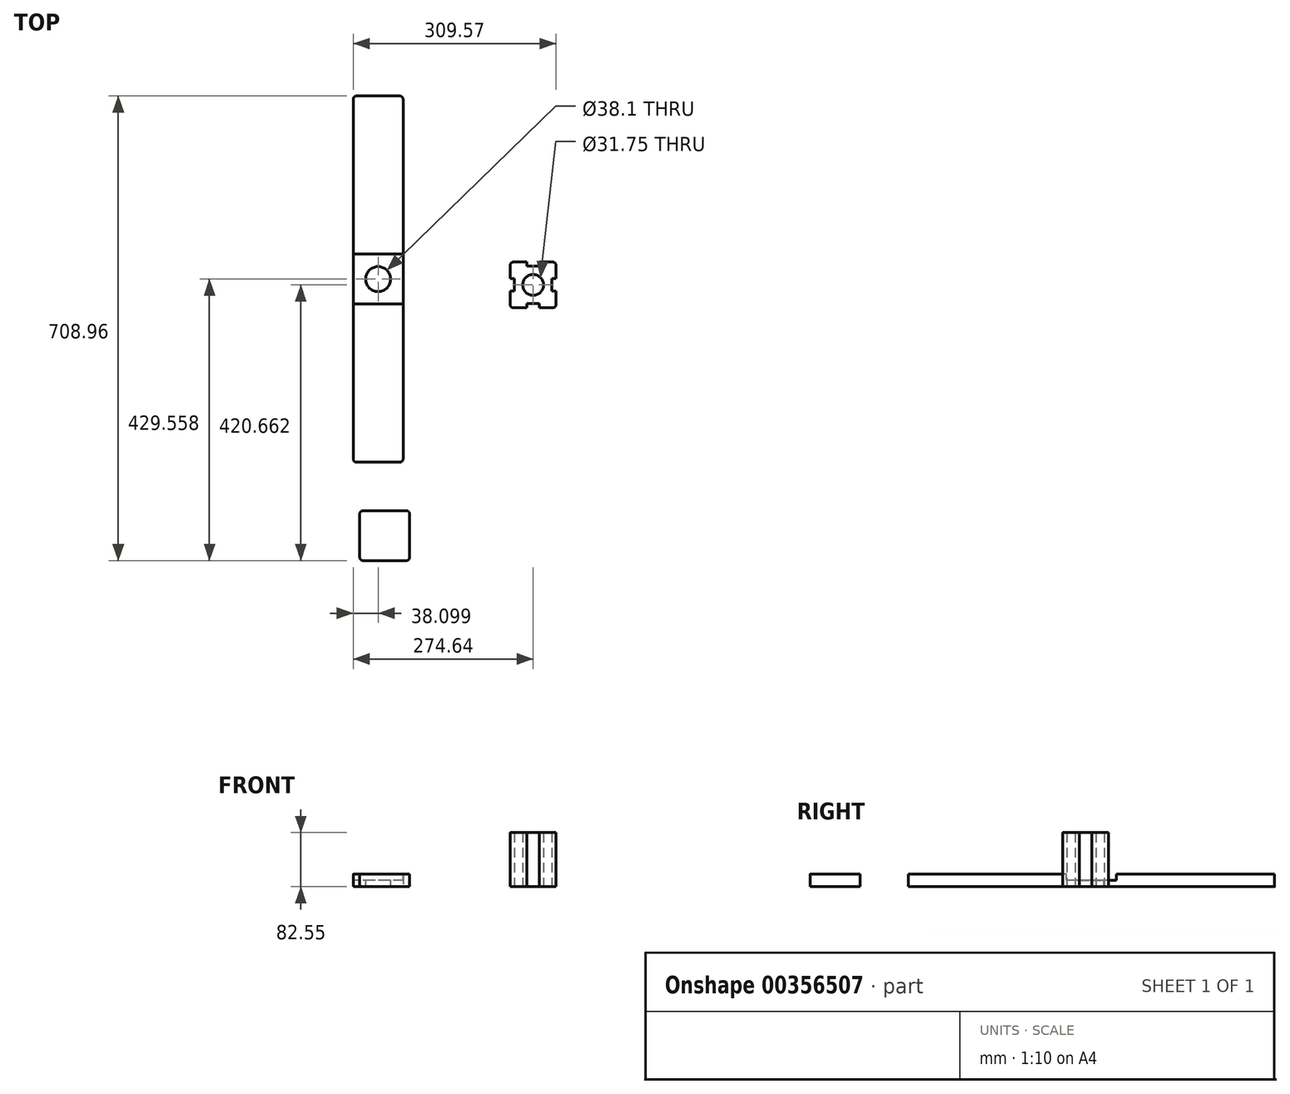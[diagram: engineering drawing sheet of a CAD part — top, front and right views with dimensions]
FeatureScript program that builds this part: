
annotation { "Feature Type Name" : "Feature", "Feature Type Description" : "" }
export const myFeature = defineFeature(function(context is Context, id is Id, definition is map)
    precondition{}
    {
        {
            assignVariable(context, id + "F0", {"name" : "BaseThickness", "anyValue" : 19.05 * mm});
        }
        {
            var Q0;
            Q0=qCreatedBy(makeId("Top.planeOp"),FACE);
            var sketch = newSketch(context, id + "F1", { "sketchPlane" : qUnion([Q0])});
            skLineSegment(sketch, "E0.bottom", {"start": v(32.09, 39.46) * mm, "end": v(57.49, 39.46) * mm});
            skLineSegment(sketch, "E0.top", {"start": v(32.09, -30.4) * mm, "end": v(57.49, -30.4) * mm});
            skLineSegment(sketch, "E0.left", {"start": v(32.09, 39.46) * mm, "end": v(32.09, 14.06) * mm});
            skLineSegment(sketch, "E0.right", {"start": v(101.94, 39.46) * mm, "end": v(101.94, 14.06) * mm});
            skLineSegment(sketch, "E1", {"start": v(32.09, 39.46) * mm, "end": v(101.94, -30.4) * mm, "construction": true});
            skCircle(sketch, "E2", {"center": v(67.01, 4.53) * mm, "radius": 15.88 * mm});
            skLineSegment(sketch, "E3.top", {"start": v(57.49, 33.1) * mm, "end": v(76.54, 33.1) * mm});
            skLineSegment(sketch, "E3.left", {"start": v(57.49, 39.46) * mm, "end": v(57.49, 33.1) * mm});
            skLineSegment(sketch, "E3.right", {"start": v(76.54, 39.46) * mm, "end": v(76.54, 33.1) * mm});
            skPoint(sketch, "E4", {"position": v(67.01, 39.46) * mm});
            skPoint(sketch, "E5", {"position": v(101.94, 4.53) * mm});
            skPoint(sketch, "E6", {"position": v(67.01, -30.4) * mm});
            skLineSegment(sketch, "E7.bottom", {"start": v(95.59, 14.06) * mm, "end": v(101.94, 14.06) * mm});
            skLineSegment(sketch, "E7.top", {"start": v(95.59, -5) * mm, "end": v(101.94, -5) * mm});
            skLineSegment(sketch, "E7.left", {"start": v(95.59, 14.06) * mm, "end": v(95.59, -5) * mm});
            skLineSegment(sketch, "E8.bottom", {"start": v(57.49, -24.04) * mm, "end": v(76.54, -24.04) * mm});
            skLineSegment(sketch, "E8.left", {"start": v(57.49, -24.04) * mm, "end": v(57.49, -30.4) * mm});
            skLineSegment(sketch, "E8.right", {"start": v(76.54, -24.04) * mm, "end": v(76.54, -30.4) * mm});
            skLineSegment(sketch, "E9.bottom", {"start": v(32.09, 14.06) * mm, "end": v(38.44, 14.06) * mm});
            skLineSegment(sketch, "E9.top", {"start": v(32.09, -5) * mm, "end": v(38.44, -5) * mm});
            skLineSegment(sketch, "E9.right", {"start": v(38.44, 14.06) * mm, "end": v(38.44, -5) * mm});
            skLineSegment(sketch, "E10.trimOffspring", {"start": v(76.54, 39.46) * mm, "end": v(101.94, 39.46) * mm});
            skLineSegment(sketch, "E11.trimOffspring", {"start": v(101.94, -5) * mm, "end": v(101.94, -30.4) * mm});
            skLineSegment(sketch, "E12.trimOffspring", {"start": v(76.54, -30.4) * mm, "end": v(101.94, -30.4) * mm});
            skLineSegment(sketch, "E13.trimOffspring", {"start": v(32.09, -5) * mm, "end": v(32.09, -30.4) * mm});
            skSolve(sketch);
        }
        {
            var Q0;
            Q0 = qSketchRegion(id + "F1", true);
            extrude(context, id + "F2", {"entities" : qUnion([Q0]), "depth" : 82.55 * mm});
        }
        {
            var Q0;
            Q0=qCreatedBy(makeId("Top.planeOp"),FACE);
            var sketch = newSketch(context, id + "F3", { "sketchPlane" : qUnion([Q0])});
            skLineSegment(sketch, "E14.bottom", {"start": v(-131.43, 292.83) * mm, "end": v(-207.63, 292.83) * mm});
            skLineSegment(sketch, "E14.top", {"start": v(-131.43, -265.97) * mm, "end": v(-207.63, -265.97) * mm});
            skLineSegment(sketch, "E14.left", {"start": v(-131.43, 292.83) * mm, "end": v(-131.43, -265.97) * mm});
            skLineSegment(sketch, "E14.right", {"start": v(-207.63, 292.83) * mm, "end": v(-207.63, -265.97) * mm});
            skLineSegment(sketch, "E15.bottom", {"start": v(-197.64, -339.93) * mm, "end": v(-121.44, -339.93) * mm});
            skLineSegment(sketch, "E15.top", {"start": v(-197.64, -416.13) * mm, "end": v(-121.44, -416.13) * mm});
            skLineSegment(sketch, "E15.left", {"start": v(-197.64, -339.93) * mm, "end": v(-197.64, -416.13) * mm});
            skLineSegment(sketch, "E15.right", {"start": v(-121.44, -339.93) * mm, "end": v(-121.44, -416.13) * mm});
            skSolve(sketch);
        }
        {
            var Q0;
            Q0 = qSketchRegion(id + "F3", true);
            extrude(context, id + "F4", {"entities" : qUnion([Q0]), "depth" : getVariable(context, 'BaseThickness')});
        }
        {
            var Q0;
            Q0=makeQuery(id+"F4.opExtrude","CAP_FACE",FACE,{"disambiguationData":[OSD([sQuery(id+"F3.wireOp",EDGE,"E14.bottom"),sQuery(id+"F3.wireOp",EDGE,"E14.top"),sQuery(id+"F3.wireOp",EDGE,"E14.left"),sQuery(id+"F3.wireOp",EDGE,"E14.right")])],"isStart":false});
            var sketch = newSketch(context, id + "F5", { "sketchPlane" : qUnion([Q0])});
            skLineSegment(sketch, "E16", {"start": v(-169.53, 292.83) * mm, "end": v(-169.53, -265.97) * mm, "construction": true});
            skPoint(sketch, "E17", {"position": v(-169.53, 13.43) * mm});
            skLineSegment(sketch, "E18", {"start": v(-131.43, 51.53) * mm, "end": v(-207.63, 51.53) * mm});
            skLineSegment(sketch, "E19", {"start": v(-131.43, 13.43) * mm, "end": v(-169.53, 13.43) * mm, "construction": true});
            skLineSegment(sketch, "E20.MirrorCS", {"start": v(-131.43, -24.67) * mm, "end": v(-207.63, -24.67) * mm});
            skLineSegment(sketch, "E21", {"start": v(-155.5, 51.53) * mm, "end": v(-155.5, -24.67) * mm, "construction": true});
            skPoint(sketch, "E22", {"position": v(-155.5, 13.43) * mm});
            skCircle(sketch, "E23", {"center": v(-169.53, 13.43) * mm, "radius": 19.05 * mm});
            skSolve(sketch);
        }
        {
            var Q0;
            Q0 = qSketchRegion(id + "F5", true);
            var Q1;
            {var subQ0=sQuery(id+"F5.wireOp",EDGE,"E18");Q1=makeQuery(id+"F5.imprint","IMPRINT",FACE,{"disambiguationData":[TD([[makeQuery(id+"F5.imprint","IMPRINT",EDGE,{"derivedFrom":subQ0}),1.0]])]});}
            extrude(context, id + "F6", {"entities" : qUnion([Q0, Q1]), "operationType" : NewBodyOperationType.REMOVE, "oppositeDirection" : true, "depth" : getVariable(context, 'BaseThickness') / 2});
        }
        {
            var Q0;
            Q0=makeQuery(id+"F4.opExtrude","SWEPT_EDGE",EDGE,{"disambiguationData":[OSD([sQuery(id+"F3.wireOp",EDGE,"E14.bottom"),sQuery(id+"F3.wireOp",EDGE,"E14.right")])]});
            var Q1;
            Q1=makeQuery(id+"F4.opExtrude","SWEPT_EDGE",EDGE,{"disambiguationData":[OSD([sQuery(id+"F3.wireOp",EDGE,"E14.bottom"),sQuery(id+"F3.wireOp",EDGE,"E14.left")])]});
            var Q2;
            Q2=makeQuery(id+"F4.opExtrude","SWEPT_EDGE",EDGE,{"disambiguationData":[OSD([sQuery(id+"F3.wireOp",EDGE,"E14.top"),sQuery(id+"F3.wireOp",EDGE,"E14.right")])]});
            var Q3;
            Q3=makeQuery(id+"F4.opExtrude","SWEPT_EDGE",EDGE,{"disambiguationData":[OSD([sQuery(id+"F3.wireOp",EDGE,"E14.top"),sQuery(id+"F3.wireOp",EDGE,"E14.left")])]});
            fillet(context, id + "F7", {"entities" : qUnion([Q0, Q1, Q2, Q3]), "radius" : 5.08 * mm, "tangentPropagation" : true, "allowEdgeOverflow" : false});
        }
        {
            var Q0;
            Q0=makeQuery(id+"F2.opExtrude","SWEPT_EDGE",EDGE,{"disambiguationData":[OSD([sQuery(id+"F1.wireOp",EDGE,"E11.trimOffspring"),sQuery(id+"F1.wireOp",EDGE,"E12.trimOffspring")])]});
            var Q1;
            Q1=makeQuery(id+"F2.opExtrude","SWEPT_EDGE",EDGE,{"disambiguationData":[OSD([sQuery(id+"F1.wireOp",EDGE,"E0.top"),sQuery(id+"F1.wireOp",EDGE,"E13.trimOffspring")])]});
            var Q2;
            Q2=makeQuery(id+"F2.opExtrude","SWEPT_EDGE",EDGE,{"disambiguationData":[OSD([sQuery(id+"F1.wireOp",EDGE,"E0.right"),sQuery(id+"F1.wireOp",EDGE,"E10.trimOffspring")])]});
            var Q3;
            Q3=makeQuery(id+"F2.opExtrude","SWEPT_EDGE",EDGE,{"disambiguationData":[OSD([sQuery(id+"F1.wireOp",EDGE,"E0.bottom"),sQuery(id+"F1.wireOp",EDGE,"E0.left")])]});
            fillet(context, id + "F8", {"entities" : qUnion([Q0, Q1, Q2, Q3]), "radius" : 5.08 * mm, "tangentPropagation" : true, "allowEdgeOverflow" : false});
        }
        {
            var Q0;
            Q0=makeQuery(id+"F5.imprint","IMPRINT",FACE,{"disambiguationData":[TD([[makeQuery(id+"F5.imprint","IMPRINT",EDGE,{"derivedFrom":sQuery(id+"F5.wireOp",EDGE,"E23")}),1.0]])]});
            var Q1;
            Q1=makeQuery(id+"F4.opExtrude","CAP_FACE",FACE,{"disambiguationData":[OSD([sQuery(id+"F3.wireOp",EDGE,"E14.bottom"),sQuery(id+"F3.wireOp",EDGE,"E14.top"),sQuery(id+"F3.wireOp",EDGE,"E14.left"),sQuery(id+"F3.wireOp",EDGE,"E14.right")])],"isStart":true});
            extrude(context, id + "F9", {"entities" : qUnion([Q0]), "operationType" : NewBodyOperationType.REMOVE, "endBound" : BoundingType.UP_TO_SURFACE, "oppositeDirection" : true, "endBoundEntityFace" : qUnion([Q1]), "depth" : 25.4 * mm});
        }
        {
            var Q0;
            Q0=makeQuery(id+"F4.opExtrude","SWEPT_EDGE",EDGE,{"disambiguationData":[OSD([sQuery(id+"F3.wireOp",EDGE,"E15.top"),sQuery(id+"F3.wireOp",EDGE,"E15.left")])]});
            var Q1;
            Q1=makeQuery(id+"F4.opExtrude","SWEPT_EDGE",EDGE,{"disambiguationData":[OSD([sQuery(id+"F3.wireOp",EDGE,"E15.top"),sQuery(id+"F3.wireOp",EDGE,"E15.right")])]});
            var Q2;
            Q2=makeQuery(id+"F4.opExtrude","SWEPT_EDGE",EDGE,{"disambiguationData":[OSD([sQuery(id+"F3.wireOp",EDGE,"E15.bottom"),sQuery(id+"F3.wireOp",EDGE,"E15.right")])]});
            var Q3;
            Q3=makeQuery(id+"F4.opExtrude","SWEPT_EDGE",EDGE,{"disambiguationData":[OSD([sQuery(id+"F3.wireOp",EDGE,"E15.bottom"),sQuery(id+"F3.wireOp",EDGE,"E15.left")])]});
            fillet(context, id + "F10", {"entities" : qUnion([Q0, Q1, Q2, Q3]), "radius" : 5.08 * mm, "tangentPropagation" : true, "allowEdgeOverflow" : false});
        }
    });
